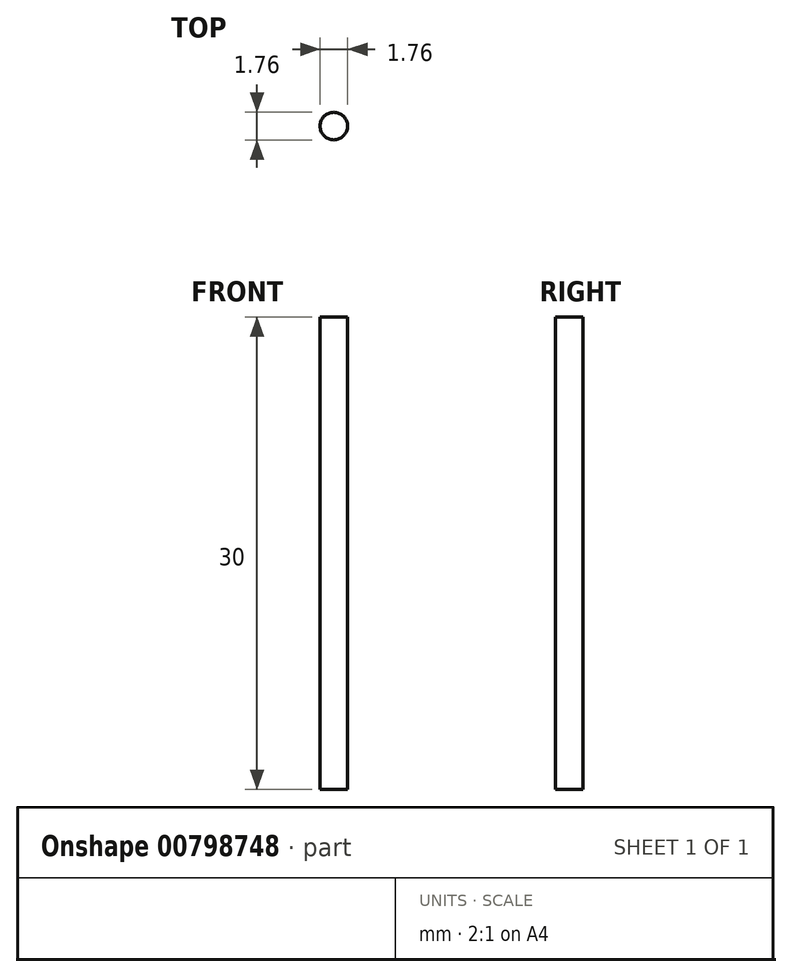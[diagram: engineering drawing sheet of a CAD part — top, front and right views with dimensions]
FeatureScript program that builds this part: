
annotation { "Feature Type Name" : "Feature", "Feature Type Description" : "" }
export const myFeature = defineFeature(function(context is Context, id is Id, definition is map)
    precondition{}
    {
        {
            var Q0;
            Q0=qCreatedBy(makeId("Top.planeOp"),FACE);
            var sketch = newSketch(context, id + "F0", { "sketchPlane" : qUnion([Q0])});
            skCircle(sketch, "E0", {"center": v(0, 0) * mm, "radius": 0.87 * mm});
            skSolve(sketch);
        }
        {
            var Q0;
            Q0=qSketchRegion(id+"F0",true);
            extrude(context, id + "F1", {"entities" : qUnion([Q0]), "endBound" : BoundingType.SYMMETRIC, "depth" : 30 * mm, "offsetDistance" : 25 * mm});
        }
    });
